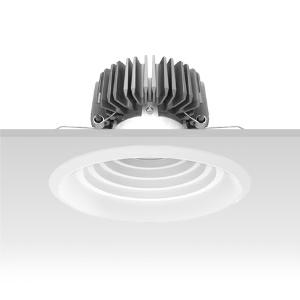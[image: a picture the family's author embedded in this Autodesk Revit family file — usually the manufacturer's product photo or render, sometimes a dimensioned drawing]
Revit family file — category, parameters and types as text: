
# Revit family: 3f_filippi_-_3f_reno_bianco_ampio_3f_filippi_-_30629_-_3f_reno_200_wh_3000-840_wide
name_source: partatom
category: Lighting Fixtures
units: mm (PartAtom-declared; Revit-internal decimal feet)

## family parameters
Cut with Voids When Loaded = No
Host = Face
Light Source = No
Part Type = Normal
Room Calculation Point = No
Round Connector Dimension = Use Diameter
Shared = No

## types (1)
- 3F Filippi - 3F Reno Bianco Ampio (1 x LED, 2635 lm, 28 W, 4000 K)
    Apparent Load = 28 VA
    Approval mark = CE
    CIE Flux Codes = 80 97 100 100 100
    Color Rendering = 80
    Color Temperature = 4000 K
    Control Gear = Electronic ballast
    Default Elevation = 1800 mm
    Description = ILLUMINOTECHNICAL
Luminous efficiency 100% (DLOR 100%, ULOR 0%).
Initial luminous flux of the luminaire 2635 lm.
Direct symmetric wide distribution.
Installation Interdistance Transv.D = 1.56 x hu - Long.D = 1.56 x hu.
Tabular UGR (CIE 117 - 4H-8H; S=0.25H; 70/50/20): RUG 20.4 - 20.4.
Beam angle: 85° - 84°.
Luminous efficacy 94 lm/W.
Lifetime (L90/B10): 30000 h. (tq+25°C)
Lifetime (L85/B10): 50000 h. (tq+25°C)
Lifetime (L70/B10): 80000 h. (tq+25°C)
Sudden decreased luminous flux after 50000 hours: 0% (C0).
Photobiological safety in compliance with IEC/TR 62778: RG0 risk exempt, (IEC 62471).
In compliance with IEC/EN 62722-2-1 - IEC/EN 62717 standards.

SOURCE
Compact LED module 3000/840.
Energy efficiency class (UE 2019/2020 - UE 2019/2015): D.
CIE 13.3 Colour rendering index: CRI >80 (R9 <50%).
IES TM-30 Fidelity Index: Rf = 84 Rg = 95.
CCT nominal colour temperature 4000 K.
Colour initial tolerance (MacAdam): SDCM 3.
Zhaga Book 3 compliant.

MECHANICAL
Passive heat dissipator in die-casting aluminium, oversized, for optimum thermal management of the LED module.
Parabolic element with graduated/concentric rings in white polycarbonate.
Transparent external lens with glossy and satin differentiated surfaces, with a cooling and anti-insect system in methacrylate (PMMA).
Fastening spring clips in stainless steel.
Dimensions: diameter 216 mm, height 142 mm. Weight 1.43 kg.
IP44 protection degree for exposed part, IP20 for recessed part.
Mechanical strength to impacts IK04 (0.5 joule).
Glow-wire test resistance 650°C.

ELECTRICAL
Wiring on a separate unit.
Halogen Free electronic wiring 230V-50/60Hz, power factor 0.95, THD <25%, constant output current, SELV, class II, 1 driver.
Power of the luminaire 28 W.
ENEC - CE.
SAFE FLICKER: PstLM=<1 and SVM=<0.4 (IEC TR 61547-1 and IEC TR 63158), to ensure a more comfortable and safe light.
Luminaire compliant with EN 60598-2-22 for power supply from a centralised emergency system CPSS (Central Power Supply System), not incorporated in the luminaire - high risk areas excluded. The default power and flux are 100% in AC and 100% in DC.
Ambient temperature from 0°C to +25°C.
Temperature class T6 max 85°C.
Relative humidity UR: <85%.

INSTALLATION
Pull-up recessed fitting.
False ceiling carving: 200 mm.
All accessories dedicated to this product are available on the Catalog and on our website www.3F-Filippi.com.

APPLICATIONS
Environments: architectural, commercial, exhibition areas, transit areas, corridors, shops, display windows, service areas.
In false ceilings with narrow voids.

WARNING
Luminaire designed for disposal/recycling at end-of-life.
Replaceable (LED only) light source by a professional. Replaceable control gear by a professional.
    Height = 0 mm  [stored 0 ft]
    Lamp = 1 x LED
    Lamp Light Flux = 2635 lm
    Lamp Power = 28 W
    Lamp count = 1
    Length = 216 mm
    Lifetime = 50000 h
    Luminous efficacy = 94 lm/W
    Manufacturer = 3F Filippi
    ModVariant = No
    Model = 3F Filippi - 30629 - 3F Reno 200 WH 3000-840 WIDE
    Mounting Place = Ceiling
    Mounting Type = Recessed
    Number of Poles = 1
    OnlyDefault = Yes
    Power Factor = 1
    Product Name = 3F Filippi - 3F Reno Bianco Ampio
    Product group = recessed luminaire
    ProductGroupID = 4
    Protection Class = Protection class II
    Protection Degree = IP 20
    RLX_Detail_Level = 1
    RLX_Emergency_Light_Flux = 0 lm
    RLX_Emergency_Type = 0
    RLX_Emergency_Type_DB = No
    RlxData = <blob elided: 92089 chars, md5=25223d6b>
    Socket = socket
    Standby Power = 0 W
    System Light Flux = 2635 lm
    System Power = 28 W
    Type Comments = Product without accessories
    Type Image = 3ffilippi_3f_reno_200_wh_2500_3000_4000.jpg
    URL = http://relux.com
    VarID = ---
    Voltage = 0 V
    Weight = 0.00 kg
    Width = 0 mm  [stored 0 ft]

note: [stored X ft] marks values corroborated as IEEE doubles in the binary element streams (Revit-internal decimal feet)

## geometry (parser evidence)
native form markers: Blend x4, Sweep x10
no freeform markers — native parametric forms only
